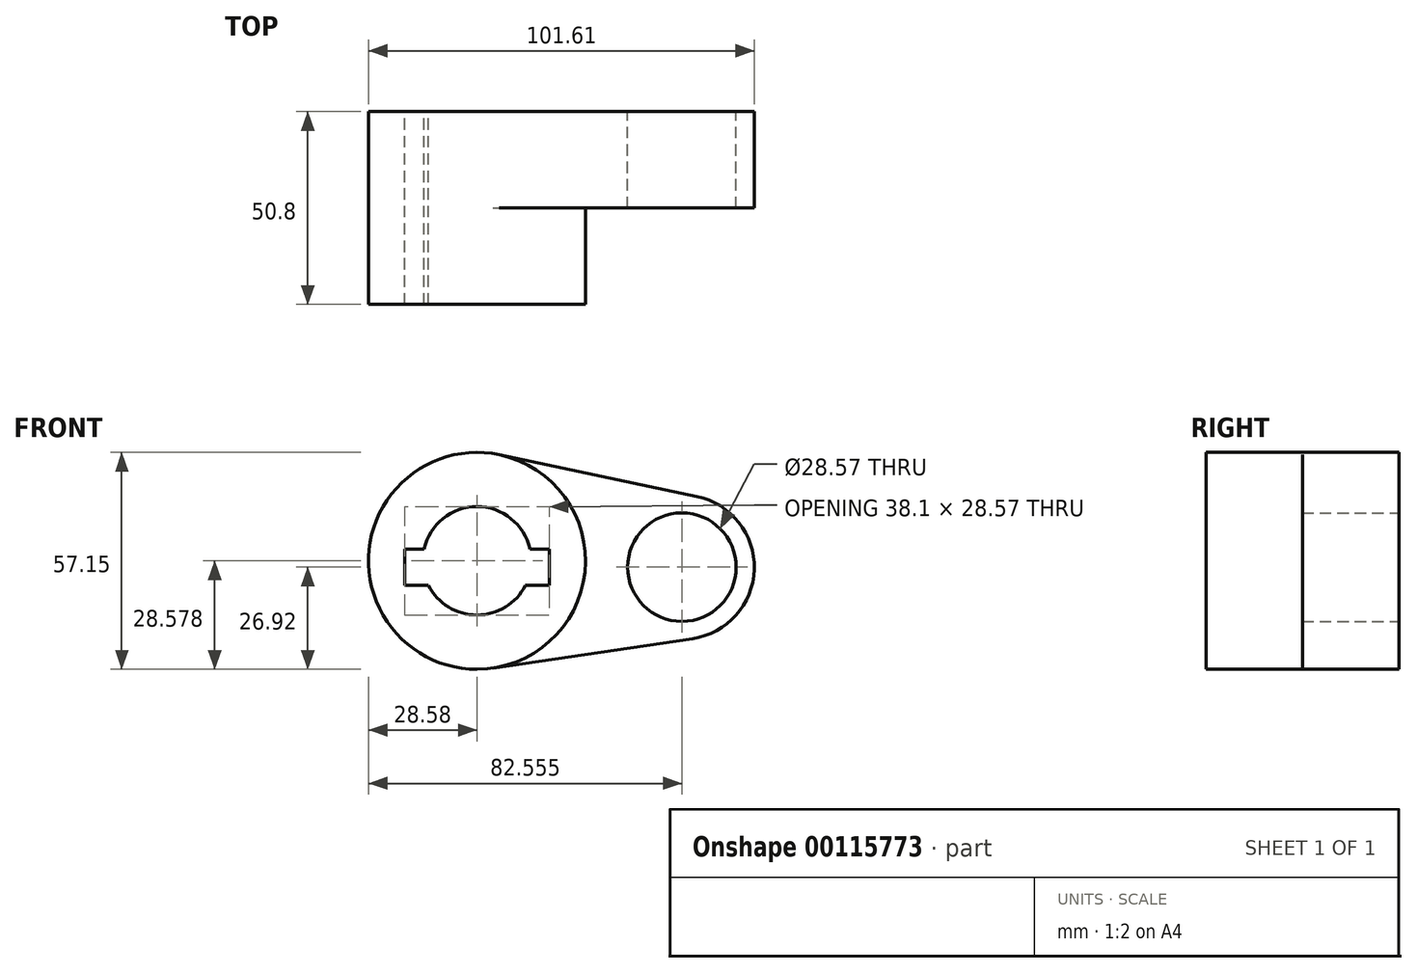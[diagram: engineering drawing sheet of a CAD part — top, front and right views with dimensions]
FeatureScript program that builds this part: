
annotation { "Feature Type Name" : "Feature", "Feature Type Description" : "" }
export const myFeature = defineFeature(function(context is Context, id is Id, definition is map)
    precondition{}
    {
        {
            var Q0;
            Q0=qCreatedBy(makeId("Front.planeOp"),FACE);
            var sketch = newSketch(context, id + "F0", { "sketchPlane" : qUnion([Q0])});
            skCircle(sketch, "E0", {"center": v(0, 1.66) * mm, "radius": 28.58 * mm});
            skCircle(sketch, "E1", {"center": v(53.98, 0) * mm, "radius": 19.05 * mm});
            skLineSegment(sketch, "E2", {"start": v(5.9, 29.62) * mm, "end": v(57.9, 18.64) * mm});
            skLineSegment(sketch, "E3", {"start": v(4.17, -26.61) * mm, "end": v(56.76, -18.85) * mm});
            skCircle(sketch, "E4", {"center": v(0, 1.66) * mm, "radius": 14.29 * mm});
            skCircle(sketch, "E5", {"center": v(53.98, 0) * mm, "radius": 14.29 * mm});
            skLineSegment(sketch, "E6.bottom", {"start": v(-19.05, 4.76) * mm, "end": v(19.05, 4.76) * mm});
            skLineSegment(sketch, "E6.top", {"start": v(-19.05, -4.76) * mm, "end": v(19.05, -4.76) * mm});
            skLineSegment(sketch, "E6.left", {"start": v(-19.05, 4.76) * mm, "end": v(-19.05, -4.76) * mm});
            skLineSegment(sketch, "E6.right", {"start": v(19.05, 4.76) * mm, "end": v(19.05, -4.76) * mm});
            skPoint(sketch, "E6.middle", {"position": v(0, 0) * mm});
            skSolve(sketch);
        }
        {
            var Q0;
            {var subQ11=sQuery(id+"F0.wireOp",EDGE,"E6.left");Q0=makeQuery(id+"F0.imprint","IMPRINT",FACE,{"disambiguationData":[TD([[makeQuery(id+"F0.imprint","IMPRINT",EDGE,{"derivedFrom":subQ11}),-1.0]])]});}
            var Q1;
            {var subQ0=sQuery(id+"F0.wireOp",EDGE,"E2");Q1=makeQuery(id+"F0.imprint","IMPRINT",FACE,{"disambiguationData":[TD([[makeQuery(id+"F0.imprint","IMPRINT",EDGE,{"derivedFrom":subQ0}),-1.0]])]});}
            var Q2;
            Q2=makeQuery(id+"F0.imprint","IMPRINT",FACE,{"disambiguationData":[TD([[makeQuery(id+"F0.imprint","IMPRINT",EDGE,{"derivedFrom":sQuery(id+"F0.wireOp",EDGE,"E5")}),-1.0]])]});
            extrude(context, id + "F1", {"entities" : qUnion([Q0, Q1, Q2]), "depth" : 25.4 * mm});
        }
        {
            var Q0;
            {var subQ11=sQuery(id+"F0.wireOp",EDGE,"E6.left");Q0=makeQuery(id+"F0.imprint","IMPRINT",FACE,{"disambiguationData":[TD([[makeQuery(id+"F0.imprint","IMPRINT",EDGE,{"derivedFrom":subQ11}),-1.0]])]});}
            extrude(context, id + "F2", {"entities" : qUnion([Q0]), "operationType" : NewBodyOperationType.ADD, "depth" : 50.8 * mm});
        }
    });
